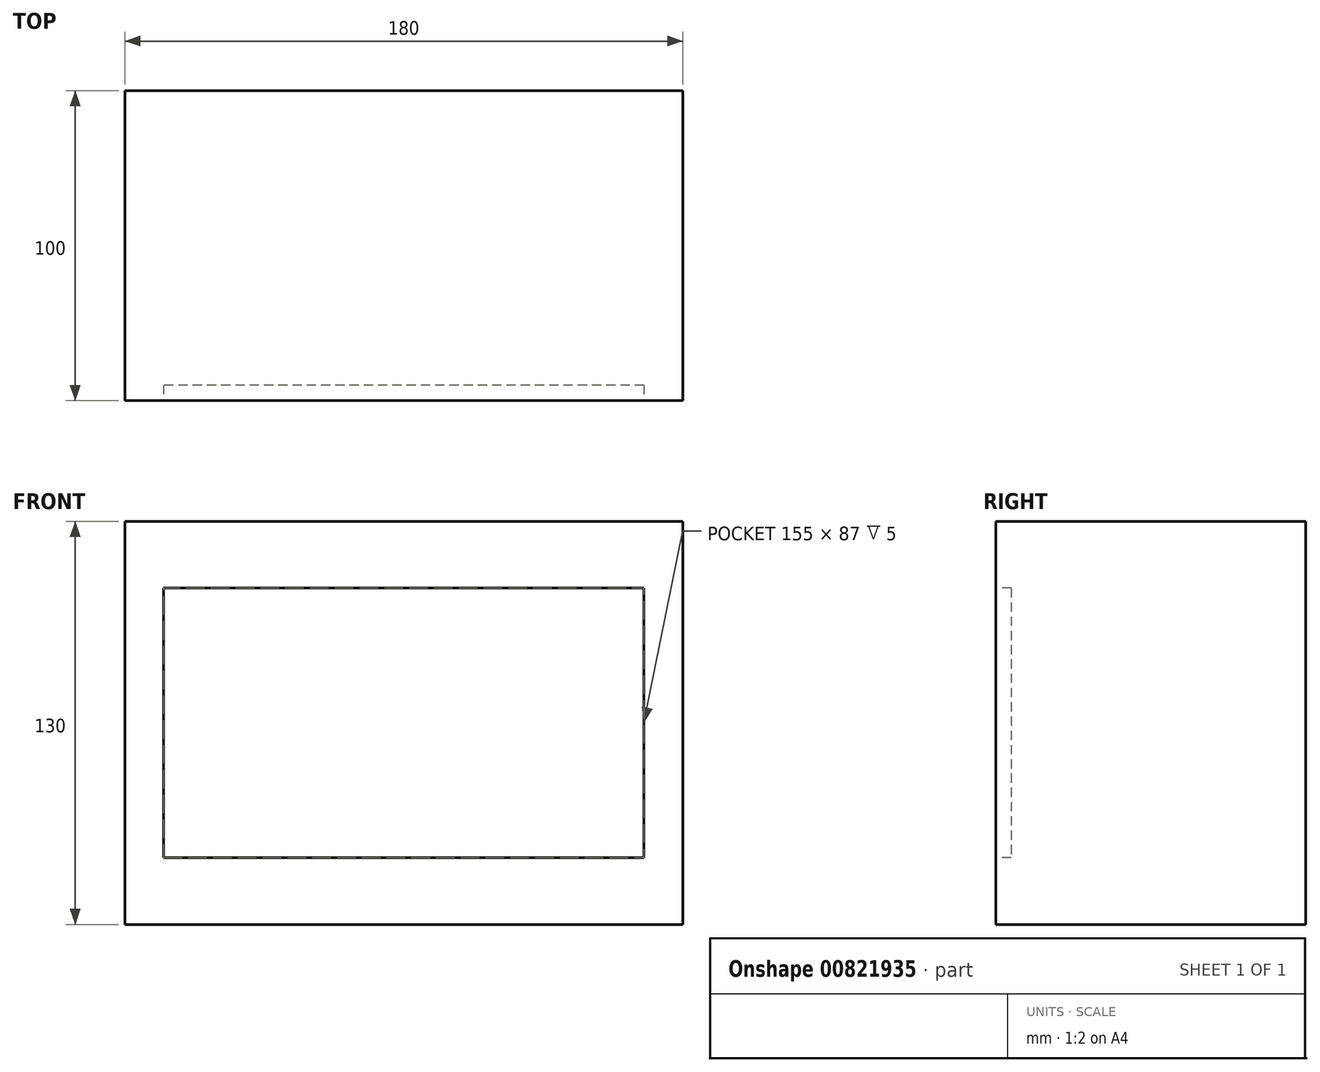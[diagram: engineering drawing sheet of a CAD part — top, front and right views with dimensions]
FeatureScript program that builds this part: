
annotation { "Feature Type Name" : "Feature", "Feature Type Description" : "" }
export const myFeature = defineFeature(function(context is Context, id is Id, definition is map)
    precondition{}
    {
        {
            var Q0;
            Q0=qCreatedBy(makeId("Front.planeOp"),FACE);
            var sketch = newSketch(context, id + "F0", { "sketchPlane" : qUnion([Q0])});
            skLineSegment(sketch, "E0.bottom", {"start": v(90, 65) * mm, "end": v(-90, 65) * mm});
            skLineSegment(sketch, "E0.top", {"start": v(90, -65) * mm, "end": v(-90, -65) * mm});
            skLineSegment(sketch, "E0.left", {"start": v(90, 65) * mm, "end": v(90, -65) * mm});
            skLineSegment(sketch, "E0.right", {"start": v(-90, 65) * mm, "end": v(-90, -65) * mm});
            skPoint(sketch, "E0.middle", {"position": v(0, 0) * mm});
            skSolve(sketch);
        }
        {
            var Q0;
            Q0=makeQuery(id+"F0.imprint","IMPRINT",FACE,{"disambiguationData":[TD([[makeQuery(id+"F0.imprint","IMPRINT",EDGE,{"derivedFrom":sQuery(id+"F0.wireOp",EDGE,"E0.bottom")}),1.0]])]});
            extrude(context, id + "F1", {"entities" : qUnion([Q0]), "oppositeDirection" : true, "depth" : 100 * mm, "offsetDistance" : 25 * mm});
        }
        {
            var Q0;
            Q0=makeQuery(id+"F1.opExtrude","CAP_FACE",FACE,{"disambiguationData":[OSD([sQuery(id+"F0.wireOp",EDGE,"E0.bottom"),sQuery(id+"F0.wireOp",EDGE,"E0.top"),sQuery(id+"F0.wireOp",EDGE,"E0.left"),sQuery(id+"F0.wireOp",EDGE,"E0.right")])],"isStart":true});
            var sketch = newSketch(context, id + "F2", { "sketchPlane" : qUnion([Q0])});
            skLineSegment(sketch, "E1.bottom", {"start": v(77.5, 43.5) * mm, "end": v(-77.5, 43.5) * mm});
            skLineSegment(sketch, "E1.top", {"start": v(77.5, -43.5) * mm, "end": v(-77.5, -43.5) * mm});
            skLineSegment(sketch, "E1.left", {"start": v(77.5, 43.5) * mm, "end": v(77.5, -43.5) * mm});
            skLineSegment(sketch, "E1.right", {"start": v(-77.5, 43.5) * mm, "end": v(-77.5, -43.5) * mm});
            skPoint(sketch, "E1.middle", {"position": v(0, 0) * mm});
            skSolve(sketch);
        }
        {
            var Q0;
            Q0=makeQuery(id+"F2.imprint","IMPRINT",FACE,{"disambiguationData":[TD([[makeQuery(id+"F2.imprint","IMPRINT",EDGE,{"derivedFrom":sQuery(id+"F2.wireOp",EDGE,"E1.bottom")}),1.0]])]});
            extrude(context, id + "F3", {"entities" : qUnion([Q0]), "operationType" : NewBodyOperationType.REMOVE, "oppositeDirection" : true, "depth" : 5 * mm, "offsetDistance" : 25 * mm});
        }
    });
